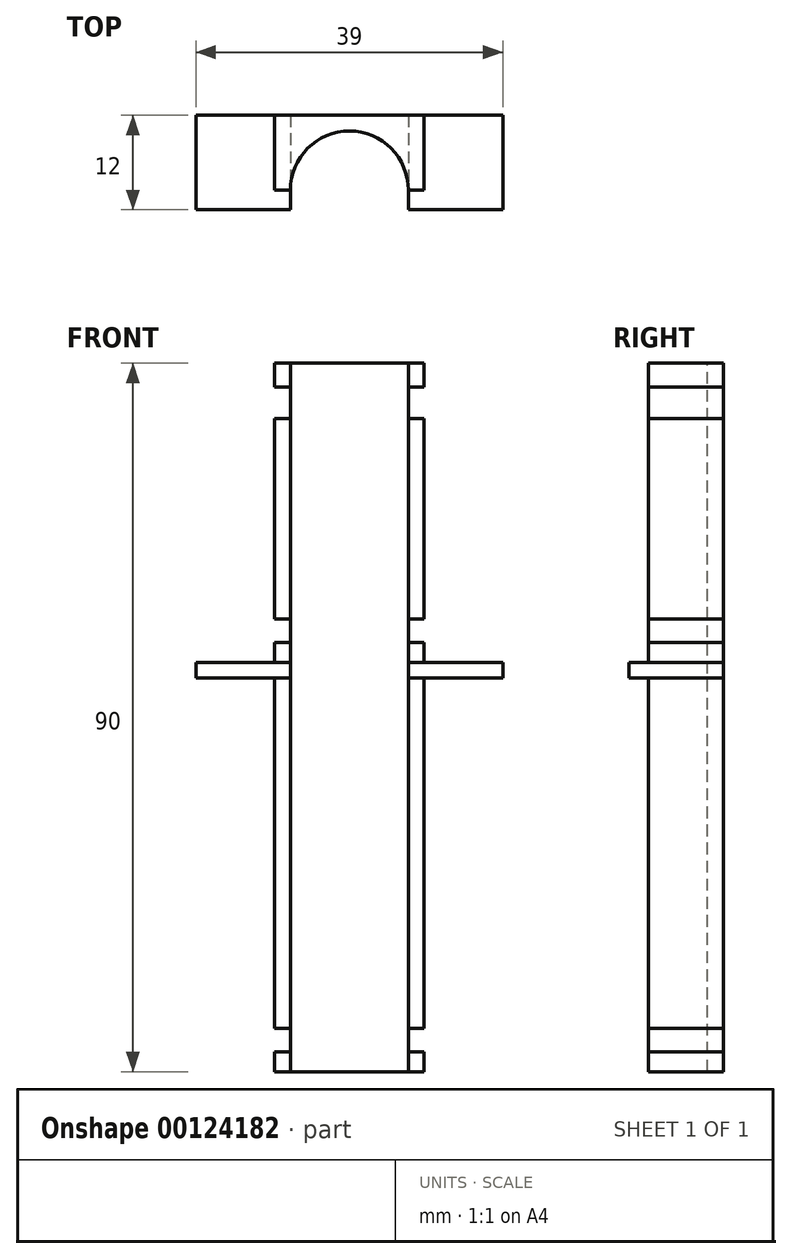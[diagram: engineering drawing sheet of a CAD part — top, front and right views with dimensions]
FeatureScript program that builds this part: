
annotation { "Feature Type Name" : "Feature", "Feature Type Description" : "" }
export const myFeature = defineFeature(function(context is Context, id is Id, definition is map)
    precondition{}
    {
        {
            var Q0;
            Q0=qCreatedBy(makeId("Top.planeOp"),FACE);
            var sketch = newSketch(context, id + "F0", { "sketchPlane" : qUnion([Q0])});
            skArc(sketch, "E0", {"start": v(-7.5, 0) * mm, "mid": v(0, 7.5) * mm, "end": v(7.5, 0) * mm});
            skLineSegment(sketch, "E1", {"start": v(-7.5, 0) * mm, "end": v(-9.5, 0) * mm});
            skLineSegment(sketch, "E2", {"start": v(7.5, 0) * mm, "end": v(9.5, 0) * mm});
            skLineSegment(sketch, "E3", {"start": v(-9.5, 0) * mm, "end": v(-9.5, 9.5) * mm});
            skLineSegment(sketch, "E4", {"start": v(-9.5, 9.5) * mm, "end": v(9.5, 9.5) * mm});
            skLineSegment(sketch, "E5", {"start": v(9.5, 9.5) * mm, "end": v(9.5, 0) * mm});
            skSolve(sketch);
        }
        {
            var Q0;
            Q0 = qSketchRegion(id + "F0", true);
            extrude(context, id + "F1", {"entities" : qUnion([Q0]), "oppositeDirection" : true, "depth" : 60 * mm});
        }
        {
            var Q0;
            Q0=qCreatedBy(makeId("Top.planeOp"),FACE);
            cPlane(context, id + "F2", {"entities" : qUnion([Q0]), "cplaneType" : CPlaneType.OFFSET, "offset" : 10 * mm, "oppositeDirection" : true, "width" : 150 * mm, "height" : 150 * mm});
        }
        {
            var Q0;
            Q0=qCreatedBy(id+"F2.planeOp",FACE);
            var sketch = newSketch(context, id + "F3", { "sketchPlane" : qUnion([Q0])});
            skLineSegment(sketch, "E6.bottom", {"start": v(-7.5, -2.5) * mm, "end": v(-19.5, -2.5) * mm});
            skLineSegment(sketch, "E6.top", {"start": v(-7.5, 9.5) * mm, "end": v(-19.5, 9.5) * mm});
            skLineSegment(sketch, "E6.left", {"start": v(-7.5, -2.5) * mm, "end": v(-7.5, 9.5) * mm});
            skLineSegment(sketch, "E6.right", {"start": v(-19.5, -2.5) * mm, "end": v(-19.5, 9.5) * mm});
            skLineSegment(sketch, "E7.MirrorCS", {"start": v(7.5, -2.5) * mm, "end": v(19.5, -2.5) * mm});
            skLineSegment(sketch, "E8.MirrorCS", {"start": v(19.5, -2.5) * mm, "end": v(19.5, 9.5) * mm});
            skLineSegment(sketch, "E9.MirrorCS", {"start": v(7.5, 9.5) * mm, "end": v(19.5, 9.5) * mm});
            skLineSegment(sketch, "E10.MirrorCS", {"start": v(7.5, -2.5) * mm, "end": v(7.5, 9.5) * mm});
            skPoint(sketch, "E11", {"position": v(0, 0) * mm});
            skSolve(sketch);
        }
        {
            var Q0;
            Q0 = qSketchRegion(id + "F3", true);
            extrude(context, id + "F4", {"entities" : qUnion([Q0]), "operationType" : NewBodyOperationType.ADD, "depth" : 2 * mm});
        }
        {
            var Q0;
            Q0=makeQuery(id+"F1.opExtrude","CAP_FACE",FACE,{"disambiguationData":[OSD([sQuery(id+"F0.wireOp",EDGE,"E0"),sQuery(id+"F0.wireOp",EDGE,"E1"),sQuery(id+"F0.wireOp",EDGE,"E2"),sQuery(id+"F0.wireOp",EDGE,"E3"),sQuery(id+"F0.wireOp",EDGE,"E4"),sQuery(id+"F0.wireOp",EDGE,"E5")])],"isStart":true});
            extrude(context, id + "F5", {"entities" : qUnion([Q0]), "operationType" : NewBodyOperationType.ADD, "depth" : 30 * mm});
        }
        {
            var Q0;
            {var subQ0=sQuery(id+"F3.wireOp",EDGE,"E6.left");var subQ2=sQuery(id+"F0.wireOp",EDGE,"E1");Q0=makeQuery(id+"F4.boolean.opBoolean","SPLIT",FACE,{"disambiguationData":[TD([makeQuery(id+"F4.opExtrude","CAP_FACE",FACE,{"disambiguationData":[OSD([sQuery(id+"F3.wireOp",EDGE,"E6.bottom"),sQuery(id+"F3.wireOp",EDGE,"E6.top"),subQ0,sQuery(id+"F3.wireOp",EDGE,"E6.right")])],"isStart":true})])],"derivedFrom":makeQuery(id+"F1.opExtrude","SWEPT_FACE",FACE,{"disambiguationData":[OSD([subQ2])]})});}
            var sketch = newSketch(context, id + "F6", { "sketchPlane" : qUnion([Q0])});
            skLineSegment(sketch, "E12.bottom", {"start": v(-9.5, -2.5) * mm, "end": v(-7.5, -2.5) * mm});
            skLineSegment(sketch, "E12.top", {"start": v(-9.5, -5.5) * mm, "end": v(-7.5, -5.5) * mm});
            skLineSegment(sketch, "E12.left", {"start": v(-9.5, -2.5) * mm, "end": v(-9.5, -5.5) * mm});
            skLineSegment(sketch, "E12.right", {"start": v(-7.5, -2.5) * mm, "end": v(-7.5, -5.5) * mm});
            skPoint(sketch, "E13", {"position": v(-9.5, -4) * mm});
            skLineSegment(sketch, "E14.0", {"start": v(-9.5, -8) * mm, "end": v(-9.5, 0) * mm});
            skLineSegment(sketch, "E15.bottom", {"start": v(-9.5, -57.5) * mm, "end": v(-7.5, -57.5) * mm});
            skLineSegment(sketch, "E15.top", {"start": v(-9.5, -54.5) * mm, "end": v(-7.5, -54.5) * mm});
            skLineSegment(sketch, "E15.left", {"start": v(-9.5, -57.5) * mm, "end": v(-9.5, -54.5) * mm});
            skLineSegment(sketch, "E15.right", {"start": v(-7.5, -57.5) * mm, "end": v(-7.5, -54.5) * mm});
            skLineSegment(sketch, "E16", {"start": v(-7.5, -5.5) * mm, "end": v(-7.5, -8) * mm});
            skLineSegment(sketch, "E17", {"start": v(-7.5, -57.5) * mm, "end": v(-7.5, -60) * mm});
            skLineSegment(sketch, "E18.MirrorCS", {"start": v(9.5, -2.5) * mm, "end": v(7.5, -2.5) * mm});
            skLineSegment(sketch, "E19.MirrorCS", {"start": v(7.5, -2.5) * mm, "end": v(7.5, -5.5) * mm});
            skLineSegment(sketch, "E20.MirrorCS", {"start": v(9.5, -5.5) * mm, "end": v(7.5, -5.5) * mm});
            skLineSegment(sketch, "E21.MirrorCS", {"start": v(9.5, -8) * mm, "end": v(9.5, 0) * mm});
            skLineSegment(sketch, "E22.MirrorCS", {"start": v(7.5, -57.5) * mm, "end": v(7.5, -54.5) * mm});
            skLineSegment(sketch, "E23.MirrorCS", {"start": v(9.5, -54.5) * mm, "end": v(7.5, -54.5) * mm});
            skLineSegment(sketch, "E24.MirrorCS", {"start": v(9.5, -57.5) * mm, "end": v(9.5, -54.5) * mm});
            skLineSegment(sketch, "E25.MirrorCS", {"start": v(9.5, -57.5) * mm, "end": v(7.5, -57.5) * mm});
            skLineSegment(sketch, "E26.bottom", {"start": v(-9.5, 27) * mm, "end": v(-7.5, 27) * mm});
            skLineSegment(sketch, "E26.top", {"start": v(-9.5, 23) * mm, "end": v(-7.5, 23) * mm});
            skLineSegment(sketch, "E26.left", {"start": v(-9.5, 27) * mm, "end": v(-9.5, 23) * mm});
            skLineSegment(sketch, "E26.right", {"start": v(-7.5, 27) * mm, "end": v(-7.5, 23) * mm});
            skLineSegment(sketch, "E27.MirrorCS", {"start": v(9.5, 23) * mm, "end": v(7.5, 23) * mm});
            skLineSegment(sketch, "E28.MirrorCS", {"start": v(9.5, 27) * mm, "end": v(9.5, 23) * mm});
            skLineSegment(sketch, "E29.MirrorCS", {"start": v(7.5, 27) * mm, "end": v(7.5, 23) * mm});
            skLineSegment(sketch, "E30.MirrorCS", {"start": v(9.5, 27) * mm, "end": v(7.5, 27) * mm});
            skSolve(sketch);
        }
        {
            var Q0;
            Q0 = qSketchRegion(id + "F6", true);
            extrude(context, id + "F7", {"entities" : qUnion([Q0]), "operationType" : NewBodyOperationType.REMOVE, "endBound" : BoundingType.THROUGH_ALL, "oppositeDirection" : true, "depth" : 25 * mm});
        }
    });
